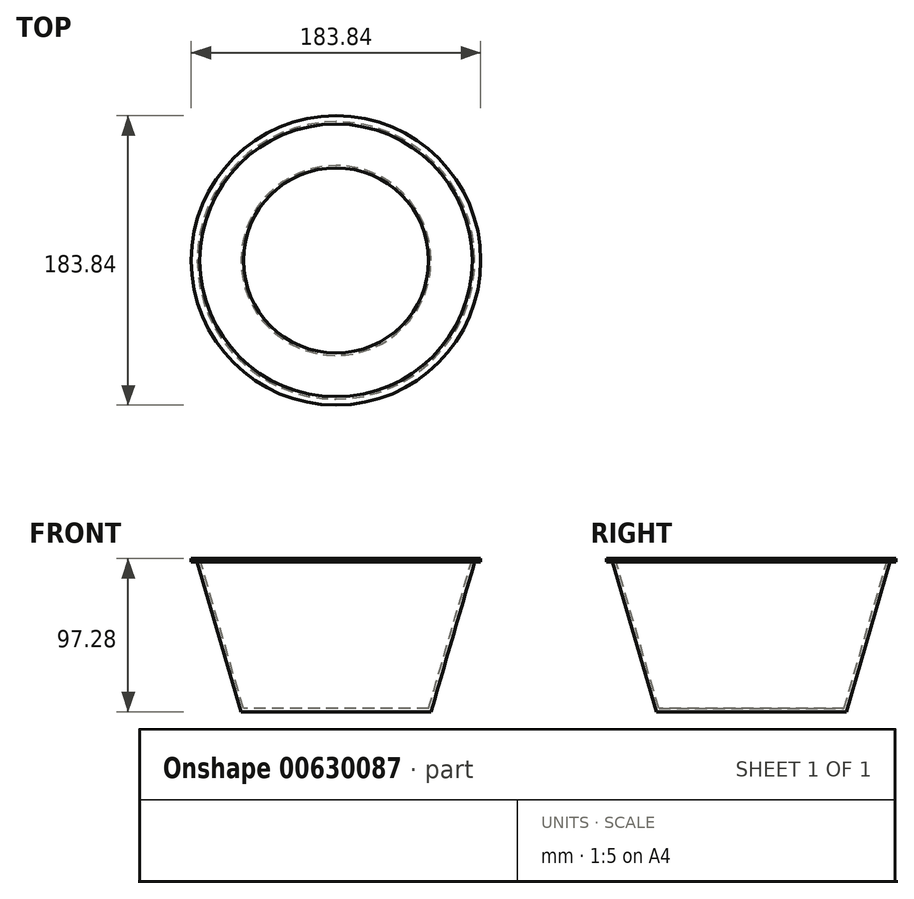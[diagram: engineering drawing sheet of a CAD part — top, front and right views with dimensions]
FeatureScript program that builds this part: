
annotation { "Feature Type Name" : "Feature", "Feature Type Description" : "" }
export const myFeature = defineFeature(function(context is Context, id is Id, definition is map)
    precondition{}
    {
        {
            var Q0;
            Q0=qCreatedBy(makeId("Front.planeOp"),FACE);
            var sketch = newSketch(context, id + "F0", { "sketchPlane" : qUnion([Q0])});
            skLineSegment(sketch, "E0", {"start": v(0, 0) * mm, "end": v(-60.33, 0) * mm});
            skLineSegment(sketch, "E1", {"start": v(-60.32, 0) * mm, "end": v(-88.1, 95.25) * mm});
            skLineSegment(sketch, "E2", {"start": v(-88.1, 95.25) * mm, "end": v(-91.92, 95.25) * mm});
            skLineSegment(sketch, "E3.0", {"start": v(-86.58, 97.28) * mm, "end": v(-91.92, 97.28) * mm});
            skLineSegment(sketch, "E3.1", {"start": v(-58.8, 2.03) * mm, "end": v(-86.58, 97.28) * mm});
            skLineSegment(sketch, "E3.2", {"start": v(0, 2.03) * mm, "end": v(-58.8, 2.03) * mm});
            skLineSegment(sketch, "E4", {"start": v(-91.92, 97.28) * mm, "end": v(-91.92, 95.25) * mm});
            skLineSegment(sketch, "E5", {"start": v(0, 2.03) * mm, "end": v(0, 0) * mm});
            skSolve(sketch);
        }
        {
            var Q0;
            Q0=makeQuery(id+"F0.imprint","IMPRINT",FACE,{"disambiguationData":[TD([[makeQuery(id+"F0.imprint","IMPRINT",EDGE,{"derivedFrom":sQuery(id+"F0.wireOp",EDGE,"E0")}),-1.0]])]});
            var Q1;
            Q1=sQuery(id+"F0.wireOp",EDGE,"E5");
            revolve(context, id + "F1", {"entities" : qUnion([Q0]), "axis" : qUnion([Q1]), "revolveType" : RevolveType.FULL});
        }
    });
